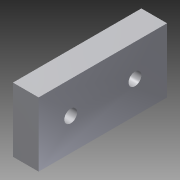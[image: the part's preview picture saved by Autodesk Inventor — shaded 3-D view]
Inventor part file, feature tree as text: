
AUTODESK INVENTOR PART (.ipt)
format: ipt  version: 2013 (Build 170138000, 138)  size: 89,088 bytes
history: native  units: mm
features: sketch x2, other x1, extrude x1, hole x1
ambient origin geometry x8: Origin, YZ Plane, XZ Plane, XY Plane, X Axis, Y Axis, Z Axis, Center Point
feature tree (5):
  other  "ソリッド1"
  extrude  "押し出し1"  Depth=20.0mm
  hole  "穴1"  [1 undecoded]
  sketch  "スケッチ1"
  sketch  "スケッチ2"
note: 1 required parameter value undecoded (feature->parameter linkage not recoverable at this tier; creation-order binding heuristic only, values carry confidence <= 0.55)
